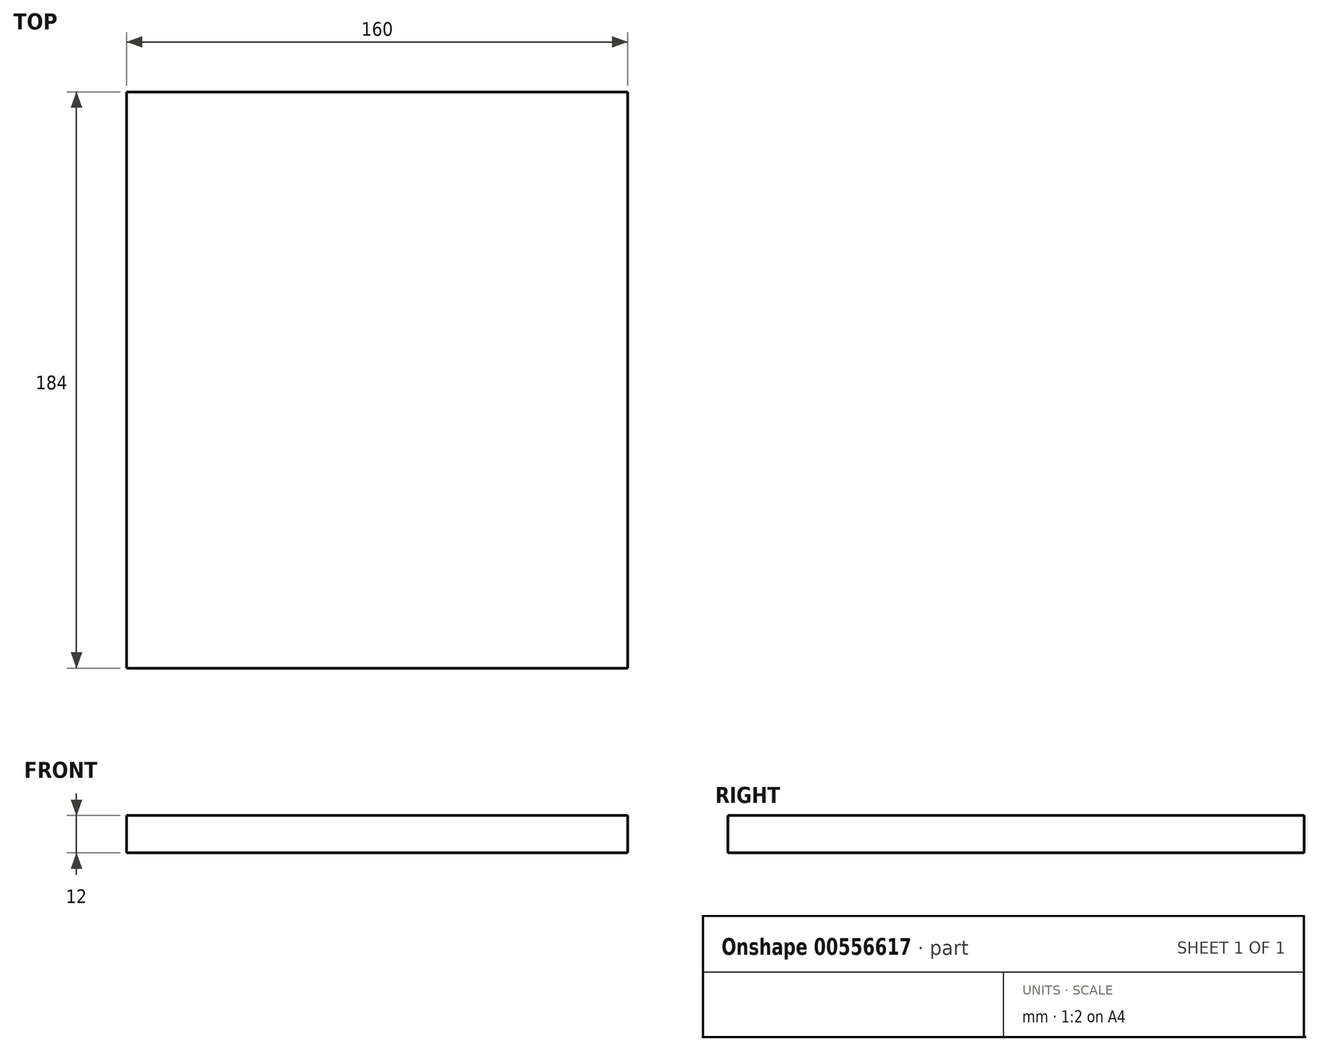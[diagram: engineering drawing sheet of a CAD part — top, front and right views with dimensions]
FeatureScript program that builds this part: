
annotation { "Feature Type Name" : "Feature", "Feature Type Description" : "" }
export const myFeature = defineFeature(function(context is Context, id is Id, definition is map)
    precondition{}
    {
        {
            var Q0;
            Q0=qCreatedBy(makeId("Top.planeOp"),FACE);
            var sketch = newSketch(context, id + "F0", { "sketchPlane" : qUnion([Q0])});
            skLineSegment(sketch, "E0", {"start": v(0, 0) * mm, "end": v(0, 184) * mm});
            skLineSegment(sketch, "E1", {"start": v(0, 184) * mm, "end": v(160, 184) * mm});
            skLineSegment(sketch, "E2", {"start": v(160, 184) * mm, "end": v(160, 0) * mm});
            skLineSegment(sketch, "E3", {"start": v(160, 0) * mm, "end": v(0, 0) * mm});
            skSolve(sketch);
        }
        {
            var Q0;
            Q0=makeQuery(id+"F0.imprint","IMPRINT",FACE,{"disambiguationData":[TD([[makeQuery(id+"F0.imprint","IMPRINT",EDGE,{"derivedFrom":sQuery(id+"F0.wireOp",EDGE,"E0")}),-1.0]])]});
            extrude(context, id + "F1", {"entities" : qUnion([Q0]), "endBound" : BoundingType.SYMMETRIC, "depth" : 12 * mm, "offsetDistance" : 25 * mm});
        }
    });
